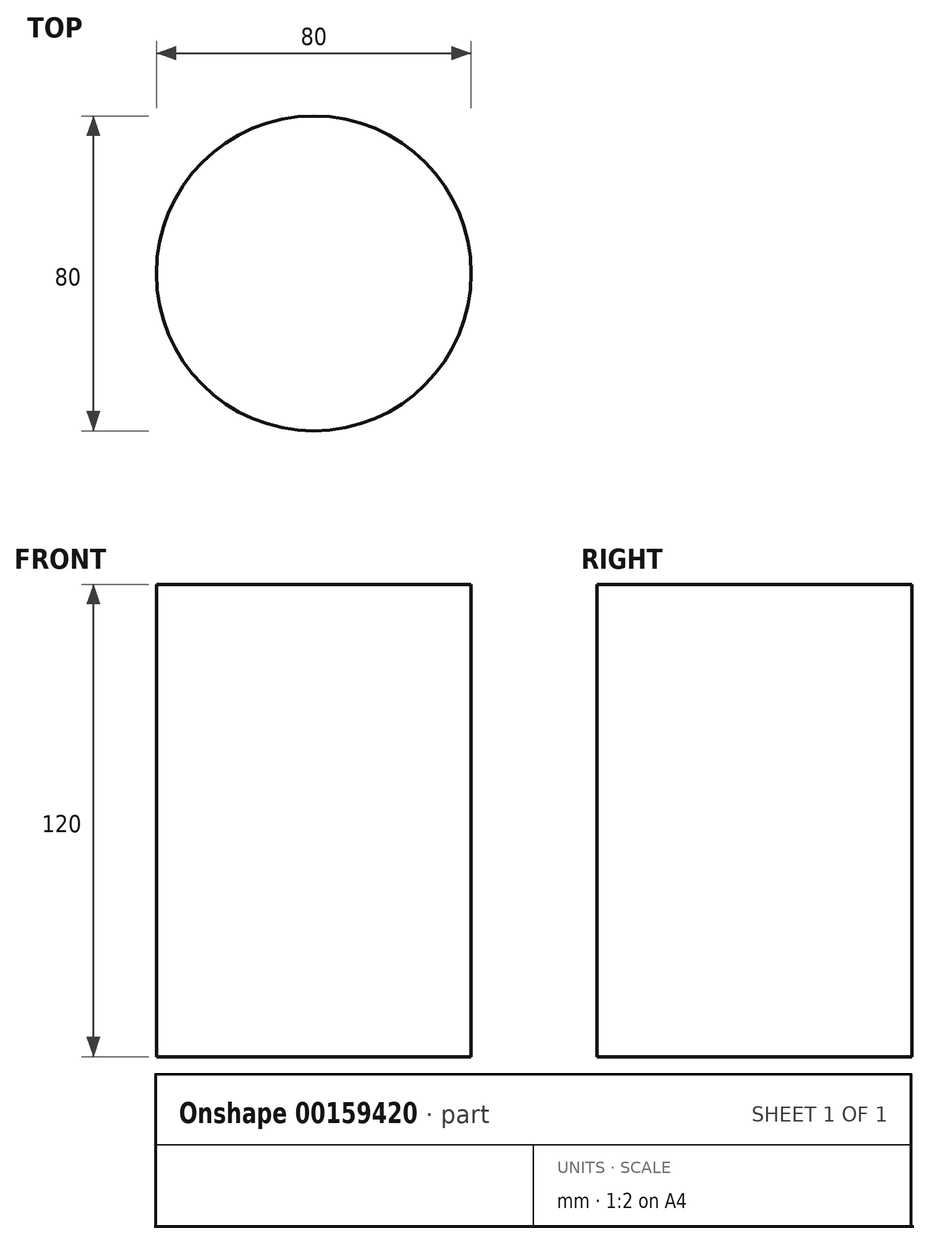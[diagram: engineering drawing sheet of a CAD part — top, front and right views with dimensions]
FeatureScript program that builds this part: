
annotation { "Feature Type Name" : "Feature", "Feature Type Description" : "" }
export const myFeature = defineFeature(function(context is Context, id is Id, definition is map)
    precondition{}
    {
        {
            var Q0;
            Q0=qCreatedBy(makeId("Top.planeOp"),FACE);
            var sketch = newSketch(context, id + "F0", { "sketchPlane" : qUnion([Q0])});
            skCircle(sketch, "E0", {"center": v(0, 0) * mm, "radius": 40 * mm});
            skSolve(sketch);
        }
        {
            var Q0;
            Q0=makeQuery(id+"F0.imprint","IMPRINT",FACE,{"disambiguationData":[TD([[makeQuery(id+"F0.imprint","IMPRINT",EDGE,{"derivedFrom":sQuery(id+"F0.wireOp",EDGE,"E0")}),1.0]])]});
            extrude(context, id + "F1", {"entities" : qUnion([Q0]), "depth" : 120 * mm});
        }
    });
